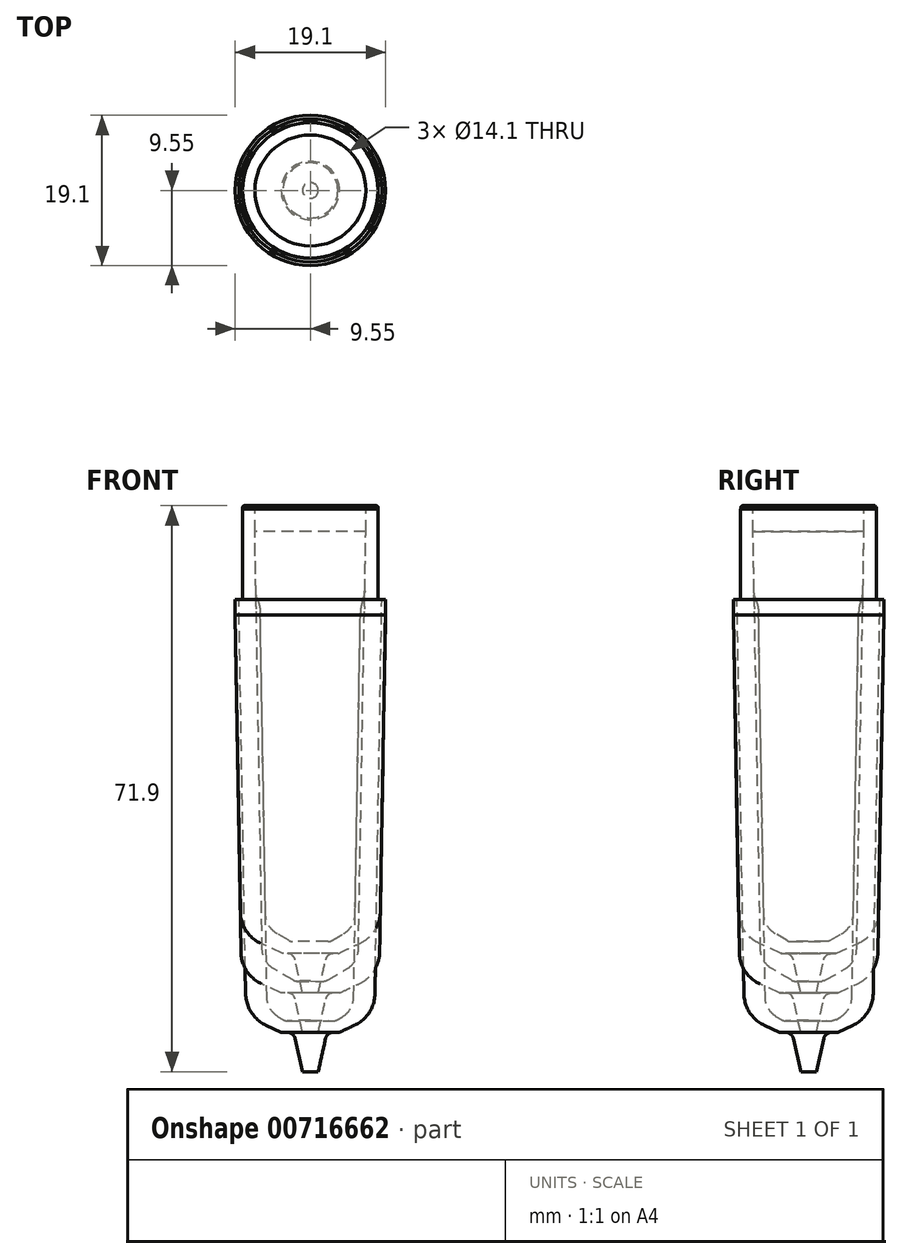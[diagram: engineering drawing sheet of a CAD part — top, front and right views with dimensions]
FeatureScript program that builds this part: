
annotation { "Feature Type Name" : "Feature", "Feature Type Description" : "" }
export const myFeature = defineFeature(function(context is Context, id is Id, definition is map)
    precondition{}
    {
        {
            var Q0;
            Q0=qCreatedBy(makeId("Front.planeOp"),FACE);
            var sketch = newSketch(context, id + "F0", { "sketchPlane" : qUnion([Q0])});
            skLineSegment(sketch, "E0", {"start": v(-9.55, 0) * mm, "end": v(-9.55, -2) * mm});
            skLineSegment(sketch, "E1", {"start": v(-9.55, -2) * mm, "end": v(-8.9, -39.7) * mm});
            skLineSegment(sketch, "E2", {"start": v(-6.3, -43.7) * mm, "end": v(-3.5, -45) * mm});
            skLineSegment(sketch, "E3", {"start": v(-3.5, -45) * mm, "end": v(-2.91, -45) * mm});
            skLineSegment(sketch, "E4", {"start": v(-1.93, -45.78) * mm, "end": v(-1, -50) * mm});
            skLineSegment(sketch, "E5", {"start": v(-1, -50) * mm, "end": v(0, -50) * mm});
            skPoint(sketch, "E6.visualSharp", {"position": v(-8.84, -42.5) * mm});
            skArc(sketch, "E6.filletArc", {"start": v(-8.9, -39.7) * mm, "mid": v(-8.17, -42.07) * mm, "end": v(-6.3, -43.7) * mm});
            skPoint(sketch, "E7.visualSharp", {"position": v(-2.1, -45) * mm});
            skArc(sketch, "E7.filletArc", {"start": v(-1.93, -45.78) * mm, "mid": v(-2.29, -45.22) * mm, "end": v(-2.91, -45) * mm});
            skSolve(sketch);
        }
        {
            var Q0;
            Q0=qCreatedBy(makeId("Front.planeOp"),FACE);
            var sketch = newSketch(context, id + "F1", { "sketchPlane" : qUnion([Q0])});
            skLineSegment(sketch, "E8", {"start": v(-8.63, 0) * mm, "end": v(-8.63, 11.5) * mm});
            skLineSegment(sketch, "E9", {"start": v(-9.55, 0) * mm, "end": v(-8.63, 0) * mm});
            skSolve(sketch);
        }
        {
            var Q0;
            Q0=qCreatedBy(makeId("Front.planeOp"),FACE);
            var sketch = newSketch(context, id + "F2", { "sketchPlane" : qUnion([Q0])});
            skLineSegment(sketch, "E10", {"start": v(0, -43.48) * mm, "end": v(-2.23, -43.48) * mm});
            skLineSegment(sketch, "E11", {"start": v(-2.73, -43.34) * mm, "end": v(-4.2, -42.5) * mm});
            skLineSegment(sketch, "E12", {"start": v(-5.7, -39.95) * mm, "end": v(-6.36, -1.76) * mm});
            skPoint(sketch, "E13.visualSharp", {"position": v(-5.66, -41.65) * mm});
            skArc(sketch, "E13.filletArc", {"start": v(-5.7, -39.95) * mm, "mid": v(-5.28, -41.42) * mm, "end": v(-4.2, -42.5) * mm});
            skPoint(sketch, "E14.visualSharp", {"position": v(-2.5, -43.48) * mm});
            skArc(sketch, "E14.filletArc", {"start": v(-2.73, -43.34) * mm, "mid": v(-2.49, -43.44) * mm, "end": v(-2.23, -43.48) * mm});
            skLineSegment(sketch, "E15", {"start": v(-6.62, -0.24) * mm, "end": v(-6.81, 0.33) * mm});
            skLineSegment(sketch, "E16", {"start": v(-7.3, 11.9) * mm, "end": v(-8.35, 11.9) * mm});
            skLineSegment(sketch, "E17", {"start": v(-8.6, 11.65) * mm, "end": v(-8.6, 11.5) * mm});
            skPoint(sketch, "E18.visualSharp", {"position": v(-8.6, 11.9) * mm});
            skArc(sketch, "E18.filletArc", {"start": v(-8.35, 11.9) * mm, "mid": v(-8.53, 11.83) * mm, "end": v(-8.6, 11.65) * mm});
            skPoint(sketch, "E19.visualSharp", {"position": v(-7.07, 11.9) * mm});
            skArc(sketch, "E19.filletArc", {"start": v(-7.05, 11.65) * mm, "mid": v(-7.12, 11.83) * mm, "end": v(-7.3, 11.9) * mm});
            skLineSegment(sketch, "E20", {"start": v(-7.05, 11.65) * mm, "end": v(-7.05, 8.6) * mm});
            skLineSegment(sketch, "E21", {"start": v(-7.05, 8.6) * mm, "end": v(-6.91, 0.93) * mm});
            skPoint(sketch, "E22.visualSharp", {"position": v(-6.9, 0.62) * mm});
            skArc(sketch, "E22.filletArc", {"start": v(-6.91, 0.93) * mm, "mid": v(-6.89, 0.62) * mm, "end": v(-6.8, 0.33) * mm});
            skPoint(sketch, "E23.visualSharp", {"position": v(-6.37, -0.98) * mm});
            skArc(sketch, "E23.filletArc", {"start": v(-6.36, -1.76) * mm, "mid": v(-6.43, -1) * mm, "end": v(-6.62, -0.24) * mm});
            skLineSegment(sketch, "E24", {"start": v(-8.6, 11.5) * mm, "end": v(-8.63, 11.5) * mm});
            skLineSegment(sketch, "E25", {"start": v(0, -43.48) * mm, "end": v(0, -50) * mm});
            skSolve(sketch);
        }
        {
            var Q0;
            Q0=qCreatedBy(makeId("Front.planeOp"),FACE);
            var sketch = newSketch(context, id + "F3", { "sketchPlane" : qUnion([Q0])});
            skArc(sketch, "E26.0", {"start": v(-8.35, 11.9) * mm, "mid": v(-8.53, 11.83) * mm, "end": v(-8.6, 11.65) * mm});
            skLineSegment(sketch, "E27.0", {"start": v(-7.3, 11.9) * mm, "end": v(-8.35, 11.9) * mm});
            skLineSegment(sketch, "E28.0", {"start": v(-8.6, 11.65) * mm, "end": v(-8.6, 11.5) * mm});
            skLineSegment(sketch, "E29.0", {"start": v(-8.6, 11.5) * mm, "end": v(-8.63, 11.5) * mm});
            skLineSegment(sketch, "E30.0", {"start": v(-8.63, 0) * mm, "end": v(-8.63, 11.5) * mm});
            skArc(sketch, "E31.0", {"start": v(-7.05, 11.65) * mm, "mid": v(-7.12, 11.83) * mm, "end": v(-7.3, 11.9) * mm});
            skLineSegment(sketch, "E32.0", {"start": v(-7.05, 11.65) * mm, "end": v(-7.05, 8.6) * mm});
            skLineSegment(sketch, "E33.0", {"start": v(-7.05, 8.6) * mm, "end": v(-6.91, 0.93) * mm});
            skArc(sketch, "E34.0", {"start": v(-6.91, 0.93) * mm, "mid": v(-6.89, 0.62) * mm, "end": v(-6.8, 0.33) * mm});
            skLineSegment(sketch, "E35.0", {"start": v(-6.62, -0.24) * mm, "end": v(-6.81, 0.33) * mm});
            skArc(sketch, "E36.0", {"start": v(-6.36, -1.76) * mm, "mid": v(-6.43, -1) * mm, "end": v(-6.62, -0.24) * mm});
            skLineSegment(sketch, "E37.0", {"start": v(-5.7, -39.95) * mm, "end": v(-6.36, -1.76) * mm});
            skLineSegment(sketch, "E38.0", {"start": v(-9.55, 0) * mm, "end": v(-8.63, 0) * mm});
            skLineSegment(sketch, "E39.0", {"start": v(-9.55, 0) * mm, "end": v(-9.55, -2) * mm});
            skLineSegment(sketch, "E40.0", {"start": v(-9.55, -2) * mm, "end": v(-8.9, -39.7) * mm});
            skArc(sketch, "E41.0", {"start": v(-5.7, -39.95) * mm, "mid": v(-5.28, -41.42) * mm, "end": v(-4.2, -42.5) * mm});
            skLineSegment(sketch, "E42.0", {"start": v(-2.73, -43.34) * mm, "end": v(-4.2, -42.5) * mm});
            skArc(sketch, "E43.0", {"start": v(-2.73, -43.34) * mm, "mid": v(-2.49, -43.44) * mm, "end": v(-2.23, -43.48) * mm});
            skLineSegment(sketch, "E44.0", {"start": v(0, -43.48) * mm, "end": v(-2.23, -43.48) * mm});
            skLineSegment(sketch, "E45.0", {"start": v(0, -43.48) * mm, "end": v(0, -50) * mm});
            skArc(sketch, "E46.0", {"start": v(-1.93, -45.78) * mm, "mid": v(-2.29, -45.22) * mm, "end": v(-2.91, -45) * mm});
            skPoint(sketch, "E47.0", {"position": v(-3.2, -45) * mm});
            skLineSegment(sketch, "E48.0", {"start": v(-3.5, -45) * mm, "end": v(-2.91, -45) * mm});
            skLineSegment(sketch, "E49.0", {"start": v(-1.93, -45.78) * mm, "end": v(-1, -50) * mm});
            skLineSegment(sketch, "E50.0", {"start": v(-1, -50) * mm, "end": v(0, -50) * mm});
            skLineSegment(sketch, "E51.0", {"start": v(-6.3, -43.7) * mm, "end": v(-3.5, -45) * mm});
            skArc(sketch, "E52.0", {"start": v(-8.9, -39.7) * mm, "mid": v(-8.17, -42.07) * mm, "end": v(-6.3, -43.7) * mm});
            skSolve(sketch);
        }
        {
            var Q0;
            Q0 = qSketchRegion(id + "F3", true);
            var Q1;
            Q1=sQuery(id+"F3.wireOp",EDGE,"E45.0");
            revolve(context, id + "F4", {"surfaceOperationType" : NewSurfaceOperationType.NEW, "entities" : qUnion([Q0]), "axis" : qUnion([Q1]), "revolveType" : RevolveType.FULL});
        }
        {
            var Q0;
            Q0=qCreatedBy(makeId("Front.planeOp"),FACE);
            var sketch = newSketch(context, id + "F5", { "sketchPlane" : qUnion([Q0])});
            skArc(sketch, "E53.0", {"start": v(-8.35, 11.9) * mm, "mid": v(-8.53, 11.83) * mm, "end": v(-8.6, 11.65) * mm});
            skLineSegment(sketch, "E54.0", {"start": v(-8.6, 11.65) * mm, "end": v(-8.6, 11.5) * mm});
            skLineSegment(sketch, "E55.0", {"start": v(-7.3, 11.9) * mm, "end": v(-8.35, 11.9) * mm});
            skArc(sketch, "E56.0", {"start": v(-7.05, 11.65) * mm, "mid": v(-7.12, 11.83) * mm, "end": v(-7.3, 11.9) * mm});
            skLineSegment(sketch, "E57.0", {"start": v(-7.05, 11.65) * mm, "end": v(-7.05, 8.6) * mm});
            skLineSegment(sketch, "E58.0", {"start": v(-7.05, 8.6) * mm, "end": v(-6.92, 1.07) * mm});
            skLineSegment(sketch, "E59.0", {"start": v(-8.63, 0) * mm, "end": v(-8.63, 11.5) * mm});
            skLineSegment(sketch, "E60.0", {"start": v(-9.55, 0) * mm, "end": v(-8.63, 0) * mm});
            skLineSegment(sketch, "E61.0", {"start": v(-9.55, 0) * mm, "end": v(-9.55, -2) * mm});
            skLineSegment(sketch, "E62.0", {"start": v(-9.55, -2) * mm, "end": v(-8.8, -44.83) * mm});
            skLineSegment(sketch, "E63", {"start": v(-3.7, -50) * mm, "end": v(-6.2, -48.83) * mm});
            skPoint(sketch, "E64.orphan", {"position": v(-8.9, -39.7) * mm});
            skArc(sketch, "E65.filletArc", {"start": v(-8.8, -44.83) * mm, "mid": v(-8.08, -47.2) * mm, "end": v(-6.2, -48.83) * mm});
            skLineSegment(sketch, "E66", {"start": v(-3.7, -50) * mm, "end": v(-2.91, -50) * mm});
            skLineSegment(sketch, "E67", {"start": v(-1.93, -50.78) * mm, "end": v(-1, -55) * mm});
            skLineSegment(sketch, "E68", {"start": v(0, -55) * mm, "end": v(-1, -55) * mm});
            skPoint(sketch, "E69.visualSharp", {"position": v(-2.1, -50) * mm});
            skArc(sketch, "E69.filletArc", {"start": v(-1.93, -50.78) * mm, "mid": v(-2.29, -50.22) * mm, "end": v(-2.91, -50) * mm});
            skLineSegment(sketch, "E70", {"start": v(-6.87, -1.21) * mm, "end": v(-6.11, -44.42) * mm});
            skLineSegment(sketch, "E71", {"start": v(-4.61, -46.96) * mm, "end": v(-2.17, -48.37) * mm});
            skLineSegment(sketch, "E72", {"start": v(-1.65, -48.5) * mm, "end": v(0, -48.48) * mm});
            skPoint(sketch, "E73.visualSharp", {"position": v(-6.08, -46.11) * mm});
            skArc(sketch, "E73.filletArc", {"start": v(-6.11, -44.42) * mm, "mid": v(-5.7, -45.89) * mm, "end": v(-4.61, -46.96) * mm});
            skPoint(sketch, "E74.visualSharp", {"position": v(-1.93, -48.51) * mm});
            skArc(sketch, "E74.filletArc", {"start": v(-2.17, -48.37) * mm, "mid": v(-1.92, -48.47) * mm, "end": v(-1.65, -48.5) * mm});
            skLineSegment(sketch, "E75", {"start": v(-6.91, 0.8) * mm, "end": v(-6.87, -0.93) * mm});
            skPoint(sketch, "E76.visualSharp", {"position": v(-6.91, 0.93) * mm});
            skArc(sketch, "E76.filletArc", {"start": v(-6.92, 1.07) * mm, "mid": v(-6.91, 0.93) * mm, "end": v(-6.91, 0.8) * mm});
            skPoint(sketch, "E77.visualSharp", {"position": v(-6.87, -1.07) * mm});
            skArc(sketch, "E77.filletArc", {"start": v(-6.87, -1.21) * mm, "mid": v(-6.87, -1.07) * mm, "end": v(-6.87, -0.93) * mm});
            skLineSegment(sketch, "E78", {"start": v(0, -48.48) * mm, "end": v(0, -55) * mm});
            skSolve(sketch);
        }
        {
            var Q0;
            Q0=qCreatedBy(makeId("Front.planeOp"),FACE);
            var sketch = newSketch(context, id + "F6", { "sketchPlane" : qUnion([Q0])});
            skLineSegment(sketch, "E79.0", {"start": v(0, -48.48) * mm, "end": v(0, -55) * mm});
            skLineSegment(sketch, "E80.0", {"start": v(-1.93, -50.78) * mm, "end": v(-1, -55) * mm});
            skLineSegment(sketch, "E81.0", {"start": v(0, -55) * mm, "end": v(-1, -55) * mm});
            skLineSegment(sketch, "E82.0", {"start": v(-1.65, -48.5) * mm, "end": v(0, -48.48) * mm});
            skArc(sketch, "E83.0", {"start": v(-2.17, -48.37) * mm, "mid": v(-1.92, -48.47) * mm, "end": v(-1.65, -48.5) * mm});
            skArc(sketch, "E84.0", {"start": v(-1.93, -50.78) * mm, "mid": v(-2.29, -50.22) * mm, "end": v(-2.91, -50) * mm});
            skLineSegment(sketch, "E85.0", {"start": v(-3.7, -50) * mm, "end": v(-2.91, -50) * mm});
            skLineSegment(sketch, "E86.0", {"start": v(-4.61, -46.96) * mm, "end": v(-2.17, -48.37) * mm});
            skLineSegment(sketch, "E87.0", {"start": v(-3.7, -50) * mm, "end": v(-6.2, -48.83) * mm});
            skArc(sketch, "E88.0", {"start": v(-6.11, -44.42) * mm, "mid": v(-5.7, -45.89) * mm, "end": v(-4.61, -46.96) * mm});
            skArc(sketch, "E89.0", {"start": v(-8.8, -44.83) * mm, "mid": v(-8.08, -47.2) * mm, "end": v(-6.2, -48.83) * mm});
            skLineSegment(sketch, "E90.0", {"start": v(-9.55, -2) * mm, "end": v(-8.8, -44.83) * mm});
            skLineSegment(sketch, "E91.0", {"start": v(-6.87, -1.21) * mm, "end": v(-6.11, -44.42) * mm});
            skLineSegment(sketch, "E92.0", {"start": v(-9.55, 0) * mm, "end": v(-9.55, -2) * mm});
            skLineSegment(sketch, "E93.0", {"start": v(-9.55, 0) * mm, "end": v(-8.63, 0) * mm});
            skLineSegment(sketch, "E94.0", {"start": v(-8.63, 0) * mm, "end": v(-8.63, 11.5) * mm});
            skArc(sketch, "E95.0", {"start": v(-6.87, -1.21) * mm, "mid": v(-6.87, -1.07) * mm, "end": v(-6.87, -0.93) * mm});
            skLineSegment(sketch, "E96.0", {"start": v(-6.91, 0.8) * mm, "end": v(-6.87, -0.93) * mm});
            skArc(sketch, "E97.0", {"start": v(-6.92, 1.07) * mm, "mid": v(-6.91, 0.93) * mm, "end": v(-6.91, 0.8) * mm});
            skLineSegment(sketch, "E98.0", {"start": v(-7.05, 8.6) * mm, "end": v(-6.92, 1.07) * mm});
            skLineSegment(sketch, "E99.0", {"start": v(-7.05, 11.65) * mm, "end": v(-7.05, 8.6) * mm});
            skArc(sketch, "E100.0", {"start": v(-7.05, 11.65) * mm, "mid": v(-7.12, 11.83) * mm, "end": v(-7.3, 11.9) * mm});
            skLineSegment(sketch, "E101.0", {"start": v(-7.3, 11.9) * mm, "end": v(-8.35, 11.9) * mm});
            skLineSegment(sketch, "E102.0", {"start": v(-8.6, 11.5) * mm, "end": v(-8.63, 11.5) * mm});
            skLineSegment(sketch, "E103.0", {"start": v(-8.6, 11.65) * mm, "end": v(-8.6, 11.5) * mm});
            skArc(sketch, "E104.0", {"start": v(-8.35, 11.9) * mm, "mid": v(-8.53, 11.83) * mm, "end": v(-8.6, 11.65) * mm});
            skSolve(sketch);
        }
        {
            var Q0;
            Q0 = qSketchRegion(id + "F6", true);
            var Q1;
            Q1=sQuery(id+"F2.wireOp",EDGE,"E25");
            revolve(context, id + "F7", {"surfaceOperationType" : NewSurfaceOperationType.NEW, "entities" : qUnion([Q0]), "axis" : qUnion([Q1]), "revolveType" : RevolveType.FULL});
        }
        {
            var Q0;
            Q0=qCreatedBy(makeId("Front.planeOp"),FACE);
            var sketch = newSketch(context, id + "F8", { "sketchPlane" : qUnion([Q0])});
            skLineSegment(sketch, "E105.0", {"start": v(-7.3, 11.9) * mm, "end": v(-8.35, 11.9) * mm});
            skArc(sketch, "E106.0", {"start": v(-7.05, 11.65) * mm, "mid": v(-7.12, 11.83) * mm, "end": v(-7.3, 11.9) * mm});
            skLineSegment(sketch, "E107.0", {"start": v(-7.05, 11.65) * mm, "end": v(-7.05, 8.6) * mm});
            skArc(sketch, "E108.0", {"start": v(-8.35, 11.9) * mm, "mid": v(-8.53, 11.83) * mm, "end": v(-8.6, 11.65) * mm});
            skPoint(sketch, "E109.0", {"position": v(-8.6, 11.58) * mm});
            skLineSegment(sketch, "E110.0", {"start": v(-8.6, 11.65) * mm, "end": v(-8.6, 11.5) * mm});
            skPoint(sketch, "E111.0", {"position": v(-8.61, 11.5) * mm});
            skLineSegment(sketch, "E112.0", {"start": v(-8.6, 11.5) * mm, "end": v(-8.63, 11.5) * mm});
            skLineSegment(sketch, "E113.0", {"start": v(-8.63, 0) * mm, "end": v(-8.63, 11.5) * mm});
            skLineSegment(sketch, "E114.0", {"start": v(-7.05, 8.6) * mm, "end": v(-6.91, 0.93) * mm});
            skPoint(sketch, "E115.0", {"position": v(-8.63, 0) * mm});
            skLineSegment(sketch, "E116", {"start": v(-8.63, 0) * mm, "end": v(-8.63, 0) * mm});
            skLineSegment(sketch, "E117", {"start": v(-5.61, -54.1) * mm, "end": v(-3.7, -55) * mm});
            skLineSegment(sketch, "E118", {"start": v(-3.7, -55) * mm, "end": v(-2.91, -55) * mm});
            skLineSegment(sketch, "E119", {"start": v(-1.93, -55.78) * mm, "end": v(-1, -60) * mm});
            skLineSegment(sketch, "E120", {"start": v(-1, -60) * mm, "end": v(0, -60) * mm});
            skPoint(sketch, "E121.visualSharp", {"position": v(-2.1, -55) * mm});
            skArc(sketch, "E121.filletArc", {"start": v(-1.93, -55.78) * mm, "mid": v(-2.29, -55.22) * mm, "end": v(-2.91, -55) * mm});
            skPoint(sketch, "E122.visualSharp", {"position": v(-8.63, -52.7) * mm});
            skArc(sketch, "E122.filletArc", {"start": v(-8.21, -50.1) * mm, "mid": v(-7.48, -52.48) * mm, "end": v(-5.61, -54.1) * mm});
            skLineSegment(sketch, "E123", {"start": v(-8.21, -50.1) * mm, "end": v(-9.08, 0) * mm});
            skLineSegment(sketch, "E124", {"start": v(-9.08, 0) * mm, "end": v(-8.63, 0) * mm});
            skLineSegment(sketch, "E125", {"start": v(0, -60) * mm, "end": v(0, -53.48) * mm});
            skLineSegment(sketch, "E126", {"start": v(0, -53.48) * mm, "end": v(-2.95, -53.53) * mm});
            skLineSegment(sketch, "E127", {"start": v(-3.47, -53.4) * mm, "end": v(-4, -53.09) * mm});
            skLineSegment(sketch, "E128", {"start": v(-5.5, -50.54) * mm, "end": v(-6.36, -1.75) * mm});
            skLineSegment(sketch, "E129", {"start": v(-6.62, -0.24) * mm, "end": v(-6.81, 0.33) * mm});
            skPoint(sketch, "E130.orphan", {"position": v(-6.91, 0.93) * mm});
            skPoint(sketch, "E131.visualSharp", {"position": v(-3.23, -53.53) * mm});
            skArc(sketch, "E131.filletArc", {"start": v(-3.47, -53.4) * mm, "mid": v(-3.22, -53.5) * mm, "end": v(-2.95, -53.53) * mm});
            skPoint(sketch, "E132.visualSharp", {"position": v(-5.48, -52.24) * mm});
            skArc(sketch, "E132.filletArc", {"start": v(-5.5, -50.54) * mm, "mid": v(-5.1, -52.01) * mm, "end": v(-4, -53.09) * mm});
            skPoint(sketch, "E133.newPointB", {"position": v(-6.91, 0.64) * mm});
            skArc(sketch, "E133.filletArc", {"start": v(-6.91, 0.93) * mm, "mid": v(-6.89, 0.63) * mm, "end": v(-6.81, 0.33) * mm});
            skPoint(sketch, "E134.visualSharp", {"position": v(-6.37, -0.98) * mm});
            skArc(sketch, "E134.filletArc", {"start": v(-6.36, -1.75) * mm, "mid": v(-6.43, -0.99) * mm, "end": v(-6.62, -0.24) * mm});
            skSolve(sketch);
        }
        {
            var Q0;
            Q0 = qSketchRegion(id + "F8", true);
            var Q1;
            Q1=sQuery(id+"F6.wireOp",EDGE,"E79.0");
            revolve(context, id + "F9", {"surfaceOperationType" : NewSurfaceOperationType.NEW, "entities" : qUnion([Q0]), "axis" : qUnion([Q1]), "revolveType" : RevolveType.FULL});
        }
    });
